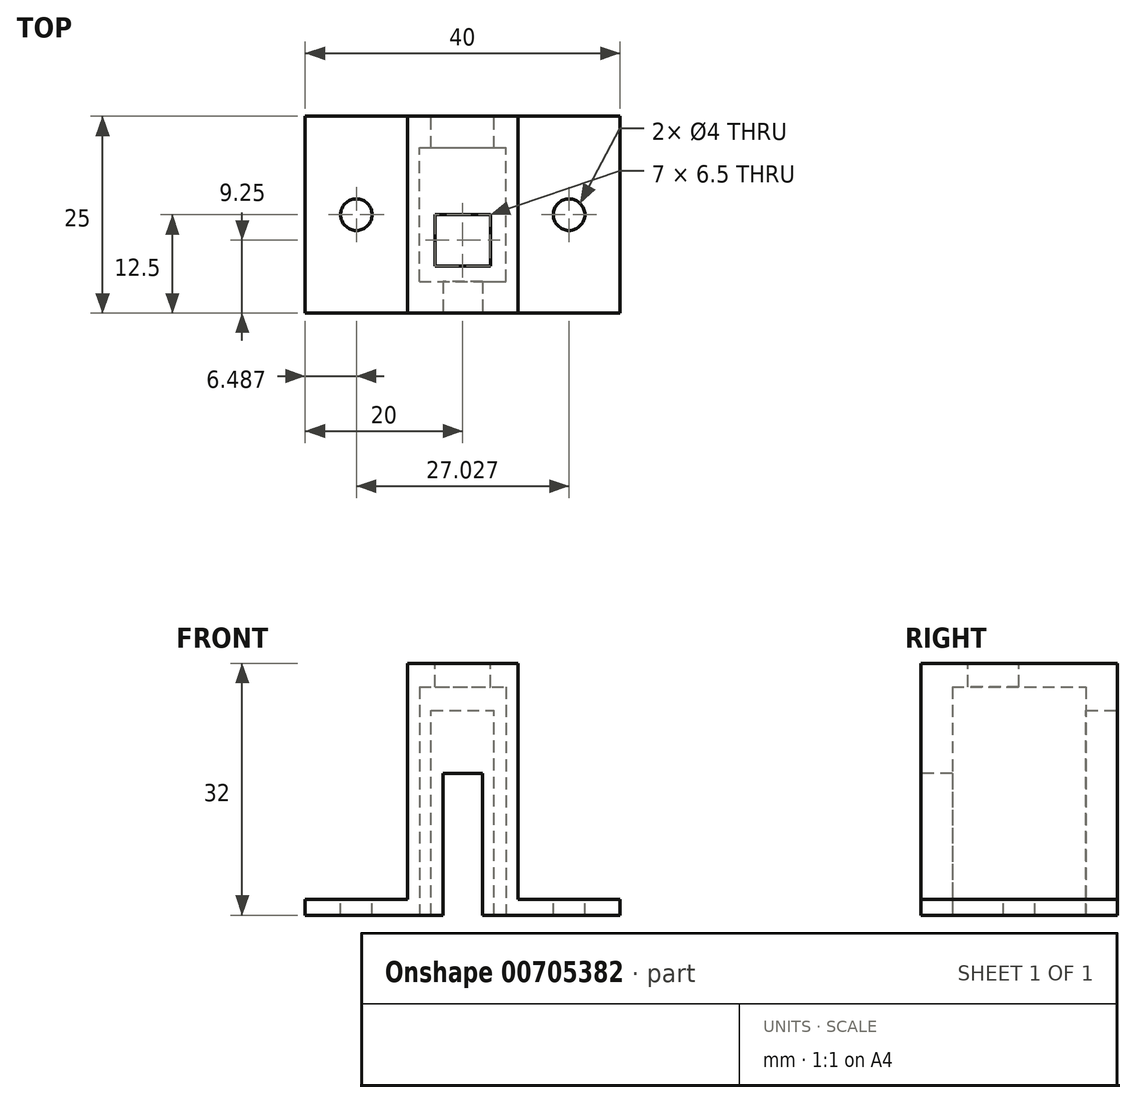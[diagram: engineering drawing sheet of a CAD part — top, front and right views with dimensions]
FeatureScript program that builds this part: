
annotation { "Feature Type Name" : "Feature", "Feature Type Description" : "" }
export const myFeature = defineFeature(function(context is Context, id is Id, definition is map)
    precondition{}
    {
        {
            var Q0;
            Q0=qCreatedBy(makeId("Top.planeOp"),FACE);
            var sketch = newSketch(context, id + "F0", { "sketchPlane" : qUnion([Q0])});
            skLineSegment(sketch, "E0.bottom", {"start": v(-20, 12.5) * mm, "end": v(20, 12.5) * mm});
            skLineSegment(sketch, "E0.top", {"start": v(-20, -12.5) * mm, "end": v(20, -12.5) * mm});
            skLineSegment(sketch, "E0.left", {"start": v(-20, 12.5) * mm, "end": v(-20, -12.5) * mm});
            skLineSegment(sketch, "E0.right", {"start": v(20, 12.5) * mm, "end": v(20, -12.5) * mm});
            skPoint(sketch, "E0.middle", {"position": v(0, 0) * mm});
            skSolve(sketch);
        }
        {
            var Q0;
            Q0=makeQuery(id+"F0.imprint","IMPRINT",FACE,{"disambiguationData":[TD([[makeQuery(id+"F0.imprint","IMPRINT",EDGE,{"derivedFrom":sQuery(id+"F0.wireOp",EDGE,"E0.bottom")}),-1.0]])]});
            extrude(context, id + "F1", {"entities" : qUnion([Q0]), "depth" : 2 * mm, "offsetDistance" : 25 * mm});
        }
        {
            var Q0;
            Q0=makeQuery(id+"F1.opExtrude","CAP_FACE",FACE,{"disambiguationData":[OSD([sQuery(id+"F0.wireOp",EDGE,"E0.bottom"),sQuery(id+"F0.wireOp",EDGE,"E0.top"),sQuery(id+"F0.wireOp",EDGE,"E0.left"),sQuery(id+"F0.wireOp",EDGE,"E0.right")])],"isStart":false});
            var sketch = newSketch(context, id + "F2", { "sketchPlane" : qUnion([Q0])});
            skLineSegment(sketch, "E1.bottom", {"start": v(-7, 12.5) * mm, "end": v(7, 12.5) * mm});
            skLineSegment(sketch, "E1.top", {"start": v(-7, -12.5) * mm, "end": v(7, -12.5) * mm});
            skLineSegment(sketch, "E1.left", {"start": v(-7, 12.5) * mm, "end": v(-7, -12.5) * mm});
            skLineSegment(sketch, "E1.right", {"start": v(7, 12.5) * mm, "end": v(7, -12.5) * mm});
            skPoint(sketch, "E1.middle", {"position": v(0, 0) * mm});
            skSolve(sketch);
        }
        {
            var Q0;
            Q0=makeQuery(id+"F2.imprint","IMPRINT",FACE,{"disambiguationData":[TD([[makeQuery(id+"F2.imprint","IMPRINT",EDGE,{"derivedFrom":sQuery(id+"F2.wireOp",EDGE,"E1.bottom")}),-1.0]])]});
            extrude(context, id + "F3", {"entities" : qUnion([Q0]), "operationType" : NewBodyOperationType.ADD, "depth" : 30 * mm, "offsetDistance" : 25 * mm});
        }
        {
            var Q0;
            {var subQ0=sQuery(id+"F0.wireOp",EDGE,"E0.top");var subQ1=sQuery(id+"F0.wireOp",EDGE,"E0.right");var subQ2=sQuery(id+"F0.wireOp",EDGE,"E0.bottom");Q0=makeQuery(id+"F3.boolean.opBoolean","SPLIT",FACE,{"disambiguationData":[TD([makeQuery(id+"F1.opExtrude","SWEPT_FACE",FACE,{"disambiguationData":[OSD([subQ1])]})])],"derivedFrom":makeQuery(id+"F1.opExtrude","CAP_FACE",FACE,{"disambiguationData":[OSD([subQ2,subQ0,sQuery(id+"F0.wireOp",EDGE,"E0.left"),subQ1])],"isStart":false})});}
            var sketch = newSketch(context, id + "F4", { "sketchPlane" : qUnion([Q0])});
            skPoint(sketch, "E2", {"position": v(13.51, 0) * mm});
            skPoint(sketch, "E3.MirrorP", {"position": v(-13.51, 0) * mm});
            skSolve(sketch);
        }
        {
            var Q0;
            Q0=sQuery(id+"F4.wireOp",VERTEX,"E2");
            var Q1;
            Q1=sQuery(id+"F4.wireOp",VERTEX,"E3.MirrorP");
            var Q2;
            Q2=makeQuery(id+"F1.opExtrude","SWEPT_BODY",BODY,{"disambiguationData":[OSD([sQuery(id+"F0.wireOp",EDGE,"E0.bottom"),sQuery(id+"F0.wireOp",EDGE,"E0.top"),sQuery(id+"F0.wireOp",EDGE,"E0.left"),sQuery(id+"F0.wireOp",EDGE,"E0.right")])]});
            hole(context, id + "F5", {"style" : HoleStyle.SIMPLE, "endStyle" : HoleEndStyle.THROUGH, "holeDiameter" : 4 * mm, "majorDiameter" : 5 * mm, "isTappedThrough" : true, "tappedDepth" : 12 * mm, "tapClearance" : 3, "locations" : qUnion([Q0, Q1]), "scope" : qUnion([Q2])});
        }
        {
            var Q0;
            Q0=makeQuery(id+"F1.opExtrude","CAP_FACE",FACE,{"disambiguationData":[OSD([sQuery(id+"F0.wireOp",EDGE,"E0.bottom"),sQuery(id+"F0.wireOp",EDGE,"E0.top"),sQuery(id+"F0.wireOp",EDGE,"E0.left"),sQuery(id+"F0.wireOp",EDGE,"E0.right")])],"isStart":true});
            var sketch = newSketch(context, id + "F6", { "sketchPlane" : qUnion([Q0])});
            skLineSegment(sketch, "E4.bottom", {"start": v(-5.5, 8.5) * mm, "end": v(5.5, 8.5) * mm});
            skLineSegment(sketch, "E4.top", {"start": v(-5.5, -8.5) * mm, "end": v(5.5, -8.5) * mm});
            skLineSegment(sketch, "E4.left", {"start": v(-5.5, 8.5) * mm, "end": v(-5.5, -8.5) * mm});
            skLineSegment(sketch, "E4.right", {"start": v(5.5, 8.5) * mm, "end": v(5.5, -8.5) * mm});
            skPoint(sketch, "E4.middle", {"position": v(0, 0) * mm});
            skSolve(sketch);
        }
        {
            var Q0;
            Q0=makeQuery(id+"F6.imprint","IMPRINT",FACE,{"disambiguationData":[TD([[makeQuery(id+"F6.imprint","IMPRINT",EDGE,{"derivedFrom":sQuery(id+"F6.wireOp",EDGE,"E4.bottom")}),-1.0]])]});
            extrude(context, id + "F7", {"entities" : qUnion([Q0]), "operationType" : NewBodyOperationType.REMOVE, "oppositeDirection" : true, "depth" : 29 * mm, "offsetDistance" : 25 * mm});
        }
        {
            var Q0;
            Q0=makeQuery(id+"F3.opExtrude","CAP_FACE",FACE,{"disambiguationData":[OSD([sQuery(id+"F2.wireOp",EDGE,"E1.bottom"),sQuery(id+"F2.wireOp",EDGE,"E1.top"),sQuery(id+"F2.wireOp",EDGE,"E1.left"),sQuery(id+"F2.wireOp",EDGE,"E1.right")])],"isStart":false});
            var sketch = newSketch(context, id + "F8", { "sketchPlane" : qUnion([Q0])});
            skLineSegment(sketch, "E5", {"start": v(0, -12.5) * mm, "end": v(0, -3.25) * mm});
            skLineSegment(sketch, "E6.bottom", {"start": v(-3.5, 0) * mm, "end": v(3.5, 0) * mm});
            skLineSegment(sketch, "E6.top", {"start": v(-3.5, -6.5) * mm, "end": v(3.5, -6.5) * mm});
            skLineSegment(sketch, "E6.left", {"start": v(-3.5, 0) * mm, "end": v(-3.5, -6.5) * mm});
            skLineSegment(sketch, "E6.right", {"start": v(3.5, 0) * mm, "end": v(3.5, -6.5) * mm});
            skPoint(sketch, "E6.middle", {"position": v(0, -3.25) * mm});
            skSolve(sketch);
        }
        {
            var Q0;
            Q0=makeQuery(id+"F8.imprint","IMPRINT",FACE,{"disambiguationData":[TD([[makeQuery(id+"F8.imprint","IMPRINT",EDGE,{"derivedFrom":sQuery(id+"F8.wireOp",EDGE,"E6.bottom")}),-1.0]])]});
            extrude(context, id + "F9", {"entities" : qUnion([Q0]), "operationType" : NewBodyOperationType.REMOVE, "oppositeDirection" : true, "depth" : 3 * mm, "offsetDistance" : 25 * mm});
        }
        {
            var Q0;
            Q0=makeQuery(id+"F3.boolean.opBoolean","MERGE",FACE,{"derivedFrom":[makeQuery(id+"F1.opExtrude","SWEPT_FACE",FACE,{"disambiguationData":[OSD([sQuery(id+"F0.wireOp",EDGE,"E0.top")])]}),makeQuery(id+"F3.opExtrude","SWEPT_FACE",FACE,{"disambiguationData":[OSD([sQuery(id+"F2.wireOp",EDGE,"E1.top")])]})]});
            var sketch = newSketch(context, id + "F10", { "sketchPlane" : qUnion([Q0])});
            skLineSegment(sketch, "E7", {"start": v(0, 0) * mm, "end": v(2.5, 0) * mm});
            skLineSegment(sketch, "E8", {"start": v(2.5, 0) * mm, "end": v(2.5, 18) * mm});
            skLineSegment(sketch, "E9.MirrorCS", {"start": v(-2.5, 0) * mm, "end": v(-2.5, 18) * mm});
            skLineSegment(sketch, "E10.MirrorCS", {"start": v(0, 0) * mm, "end": v(-2.5, 0) * mm});
            skLineSegment(sketch, "E11", {"start": v(-2.5, 18) * mm, "end": v(2.5, 18) * mm});
            skSolve(sketch);
        }
        {
            var Q0;
            Q0=makeQuery(id+"F10.imprint","IMPRINT",FACE,{"disambiguationData":[TD([[makeQuery(id+"F10.imprint","IMPRINT",EDGE,{"derivedFrom":sQuery(id+"F10.wireOp",EDGE,"E7")}),1.0]])]});
            extrude(context, id + "F11", {"entities" : qUnion([Q0]), "operationType" : NewBodyOperationType.REMOVE, "oppositeDirection" : true, "depth" : 5 * mm, "offsetDistance" : 25 * mm});
        }
        {
            var Q0;
            Q0=makeQuery(id+"F3.boolean.opBoolean","MERGE",FACE,{"derivedFrom":[makeQuery(id+"F1.opExtrude","SWEPT_FACE",FACE,{"disambiguationData":[OSD([sQuery(id+"F0.wireOp",EDGE,"E0.bottom")])]}),makeQuery(id+"F3.opExtrude","SWEPT_FACE",FACE,{"disambiguationData":[OSD([sQuery(id+"F2.wireOp",EDGE,"E1.bottom")])]})]});
            var sketch = newSketch(context, id + "F12", { "sketchPlane" : qUnion([Q0])});
            skLineSegment(sketch, "E12", {"start": v(0, 0) * mm, "end": v(4, 0) * mm});
            skLineSegment(sketch, "E13", {"start": v(4, 0) * mm, "end": v(4, 26) * mm});
            skLineSegment(sketch, "E14", {"start": v(4, 26) * mm, "end": v(0, 26) * mm});
            skLineSegment(sketch, "E15.MirrorCS", {"start": v(-4, 0) * mm, "end": v(-4, 26) * mm});
            skLineSegment(sketch, "E16.MirrorCS", {"start": v(-4, 26) * mm, "end": v(0, 26) * mm});
            skLineSegment(sketch, "E17.MirrorCS", {"start": v(0, 0) * mm, "end": v(-4, 0) * mm});
            skSolve(sketch);
        }
        {
            var Q0;
            Q0=makeQuery(id+"F12.imprint","IMPRINT",FACE,{"disambiguationData":[TD([[makeQuery(id+"F12.imprint","IMPRINT",EDGE,{"derivedFrom":sQuery(id+"F12.wireOp",EDGE,"E12")}),-1.0]])]});
            extrude(context, id + "F13", {"entities" : qUnion([Q0]), "operationType" : NewBodyOperationType.REMOVE, "oppositeDirection" : true, "depth" : 5 * mm, "offsetDistance" : 25 * mm});
        }
    });
